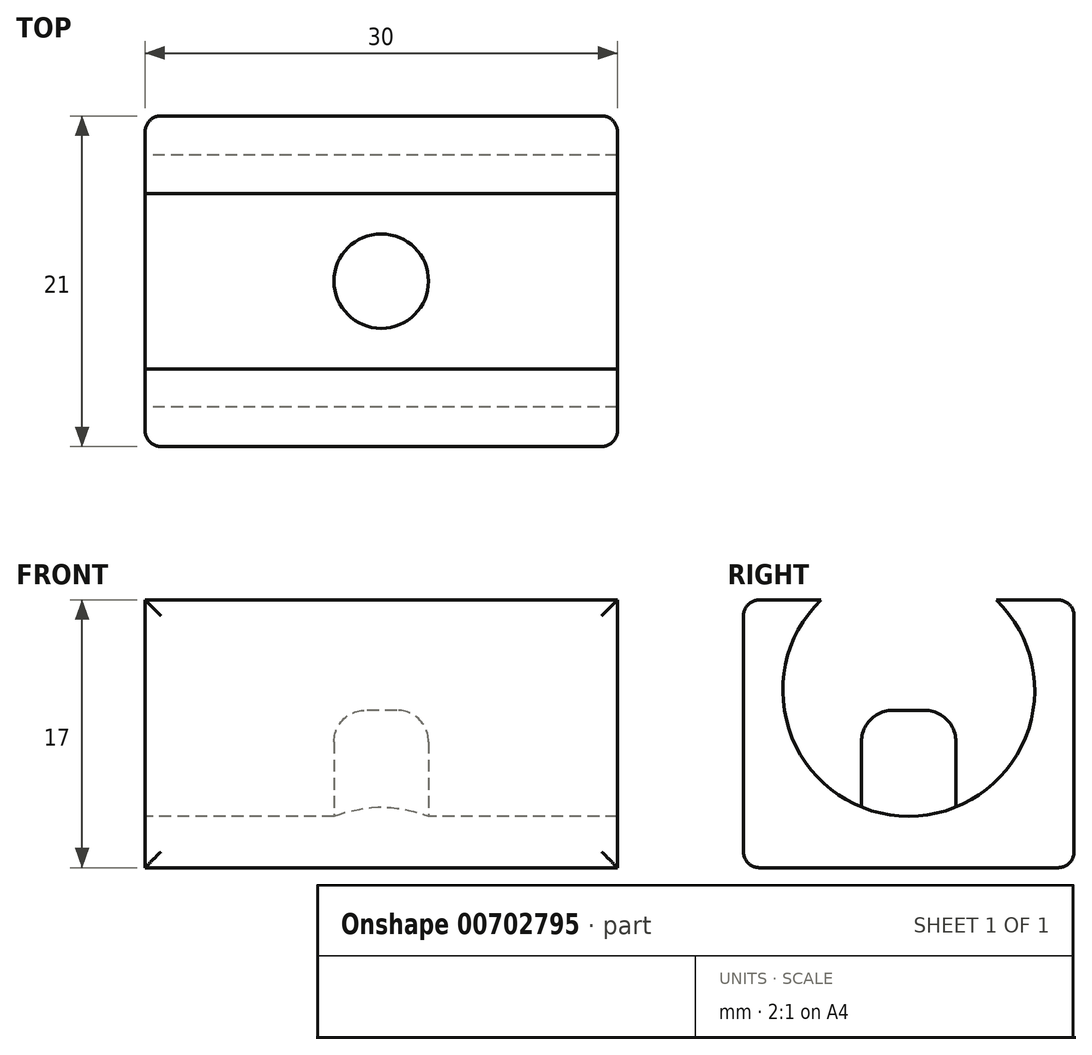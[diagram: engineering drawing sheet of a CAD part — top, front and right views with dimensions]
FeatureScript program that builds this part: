
annotation { "Feature Type Name" : "Feature", "Feature Type Description" : "" }
export const myFeature = defineFeature(function(context is Context, id is Id, definition is map)
    precondition{}
    {
        {
            var Q0;
            Q0=qCreatedBy(makeId("Top.planeOp"),FACE);
            var sketch = newSketch(context, id + "F0", { "sketchPlane" : qUnion([Q0])});
            skLineSegment(sketch, "E0.bottom", {"start": v(-15, 10.5) * mm, "end": v(15, 10.5) * mm});
            skLineSegment(sketch, "E0.top", {"start": v(-15, -10.5) * mm, "end": v(15, -10.5) * mm});
            skLineSegment(sketch, "E0.left", {"start": v(-15, 10.5) * mm, "end": v(-15, -10.5) * mm});
            skLineSegment(sketch, "E0.right", {"start": v(15, 10.5) * mm, "end": v(15, -10.5) * mm});
            skPoint(sketch, "E0.middle", {"position": v(0, 0) * mm});
            skCircle(sketch, "E1", {"center": v(0, 0) * mm, "radius": 3 * mm});
            skSolve(sketch);
        }
        {
            var Q0;
            Q0=makeQuery(id+"F0.imprint","IMPRINT",FACE,{"disambiguationData":[TD([[makeQuery(id+"F0.imprint","IMPRINT",EDGE,{"derivedFrom":sQuery(id+"F0.wireOp",EDGE,"E0.bottom")}),-1.0]])]});
            extrude(context, id + "F1", {"entities" : qUnion([Q0]), "depth" : 17 * mm, "offsetDistance" : 25 * mm});
        }
        {
            var Q0;
            Q0=makeQuery(id+"F1.opExtrude","SWEPT_FACE",FACE,{"disambiguationData":[OSD([sQuery(id+"F0.wireOp",EDGE,"E0.left")])]});
            var sketch = newSketch(context, id + "F2", { "sketchPlane" : qUnion([Q0])});
            skCircle(sketch, "E2", {"center": v(0, 11.26) * mm, "radius": 8 * mm});
            skPoint(sketch, "E3", {"position": v(0, 17) * mm});
            skSolve(sketch);
        }
        {
            var Q0;
            {var subQ0=sQuery(id+"F2.wireOp",EDGE,"E2");var subQ1=makeQuery(id+"F1.opExtrude","CAP_EDGE",EDGE,{"disambiguationData":[OSD([sQuery(id+"F0.wireOp",EDGE,"E0.left")])],"isStart":false});var subQ2=makeQuery(id+"F2.imprint","INTERSECT",VERTEX,{"disambiguationData":[OD(0.0)],"derivedFrom":[subQ1,subQ0]});Q0=makeQuery(id+"F2.imprint","IMPRINT",FACE,{"disambiguationData":[TD([[makeQuery(id+"F2.imprint","IMPRINT",EDGE,{"disambiguationData":[TD([[subQ2,-1.0]])],"derivedFrom":subQ0}),1.0]])]});}
            extrude(context, id + "F3", {"entities" : qUnion([Q0]), "operationType" : NewBodyOperationType.REMOVE, "oppositeDirection" : true, "depth" : 35 * mm, "offsetDistance" : 25 * mm});
        }
        {
            var Q0;
            Q0=makeQuery(id+"F0.imprint","IMPRINT",FACE,{"disambiguationData":[TD([[makeQuery(id+"F0.imprint","IMPRINT",EDGE,{"derivedFrom":sQuery(id+"F0.wireOp",EDGE,"E1")}),1.0]])]});
            extrude(context, id + "F4", {"entities" : qUnion([Q0]), "operationType" : NewBodyOperationType.ADD, "depth" : 10 * mm, "offsetDistance" : 25 * mm});
        }
        {
            var Q0;
            Q0=makeQuery(id+"F1.opExtrude","CAP_EDGE",EDGE,{"disambiguationData":[OSD([sQuery(id+"F0.wireOp",EDGE,"E0.top")])],"isStart":false});
            var Q1;
            Q1=makeQuery(id+"F1.opExtrude","CAP_EDGE",EDGE,{"disambiguationData":[OSD([sQuery(id+"F0.wireOp",EDGE,"E0.bottom")])],"isStart":false});
            var Q2;
            {var subQ0=sQuery(id+"F2.wireOp",EDGE,"E2");var subQ1=sQuery(id+"F0.wireOp",EDGE,"E0.left");Q2=makeQuery(id+"F3.boolean.opBoolean","COPY",EDGE,{"derivedFrom":makeQuery(id+"F3.opExtrude","SWEPT_EDGE",EDGE,{"disambiguationData":[OSD([subQ1,subQ0]),TDD([makeQuery(id+"F2.imprint","INTERSECT",VERTEX,{"disambiguationData":[OD(0.0)],"derivedFrom":[makeQuery(id+"F1.opExtrude","CAP_EDGE",EDGE,{"disambiguationData":[OSD([subQ1])],"isStart":false}),subQ0]})])]})});}
            var Q3;
            {var subQ0=sQuery(id+"F2.wireOp",EDGE,"E2");var subQ1=sQuery(id+"F0.wireOp",EDGE,"E0.left");Q3=makeQuery(id+"F3.boolean.opBoolean","COPY",EDGE,{"derivedFrom":makeQuery(id+"F3.opExtrude","SWEPT_EDGE",EDGE,{"disambiguationData":[OSD([subQ1,subQ0]),TDD([makeQuery(id+"F2.imprint","INTERSECT",VERTEX,{"disambiguationData":[OD(1.0)],"derivedFrom":[makeQuery(id+"F1.opExtrude","CAP_EDGE",EDGE,{"disambiguationData":[OSD([subQ1])],"isStart":false}),subQ0]})])]})});}
            var Q4;
            Q4=makeQuery(id+"F1.opExtrude","CAP_EDGE",EDGE,{"disambiguationData":[OSD([sQuery(id+"F0.wireOp",EDGE,"E0.top")])],"isStart":true});
            var Q5;
            Q5=makeQuery(id+"F1.opExtrude","CAP_EDGE",EDGE,{"disambiguationData":[OSD([sQuery(id+"F0.wireOp",EDGE,"E0.bottom")])],"isStart":true});
            var Q6;
            Q6=makeQuery(id+"F1.opExtrude","SWEPT_EDGE",EDGE,{"disambiguationData":[OSD([sQuery(id+"F0.wireOp",EDGE,"E0.bottom"),sQuery(id+"F0.wireOp",EDGE,"E0.left")])]});
            var Q7;
            Q7=makeQuery(id+"F1.opExtrude","SWEPT_EDGE",EDGE,{"disambiguationData":[OSD([sQuery(id+"F0.wireOp",EDGE,"E0.bottom"),sQuery(id+"F0.wireOp",EDGE,"E0.right")])]});
            var Q8;
            Q8=makeQuery(id+"F1.opExtrude","SWEPT_EDGE",EDGE,{"disambiguationData":[OSD([sQuery(id+"F0.wireOp",EDGE,"E0.top"),sQuery(id+"F0.wireOp",EDGE,"E0.right")])]});
            var Q9;
            Q9=makeQuery(id+"F1.opExtrude","SWEPT_EDGE",EDGE,{"disambiguationData":[OSD([sQuery(id+"F0.wireOp",EDGE,"E0.top"),sQuery(id+"F0.wireOp",EDGE,"E0.left")])]});
            fillet(context, id + "F5", {"entities" : qUnion([Q0, Q1, Q2, Q3, Q4, Q5, Q6, Q7, Q8, Q9]), "tangentPropagation" : true, "radius" : 1 * mm, "defaultsChanged" : false, "vertexSettings" : [], "allowEdgeOverflow" : false});
        }
        {
            var Q0;
            Q0=makeQuery(id+"F4.opExtrude","CAP_EDGE",EDGE,{"disambiguationData":[OSD([sQuery(id+"F0.wireOp",EDGE,"E1")])],"isStart":false});
            fillet(context, id + "F6", {"entities" : qUnion([Q0]), "tangentPropagation" : true, "radius" : 2 * mm, "defaultsChanged" : true, "vertexSettings" : [], "allowEdgeOverflow" : false});
        }
    });
